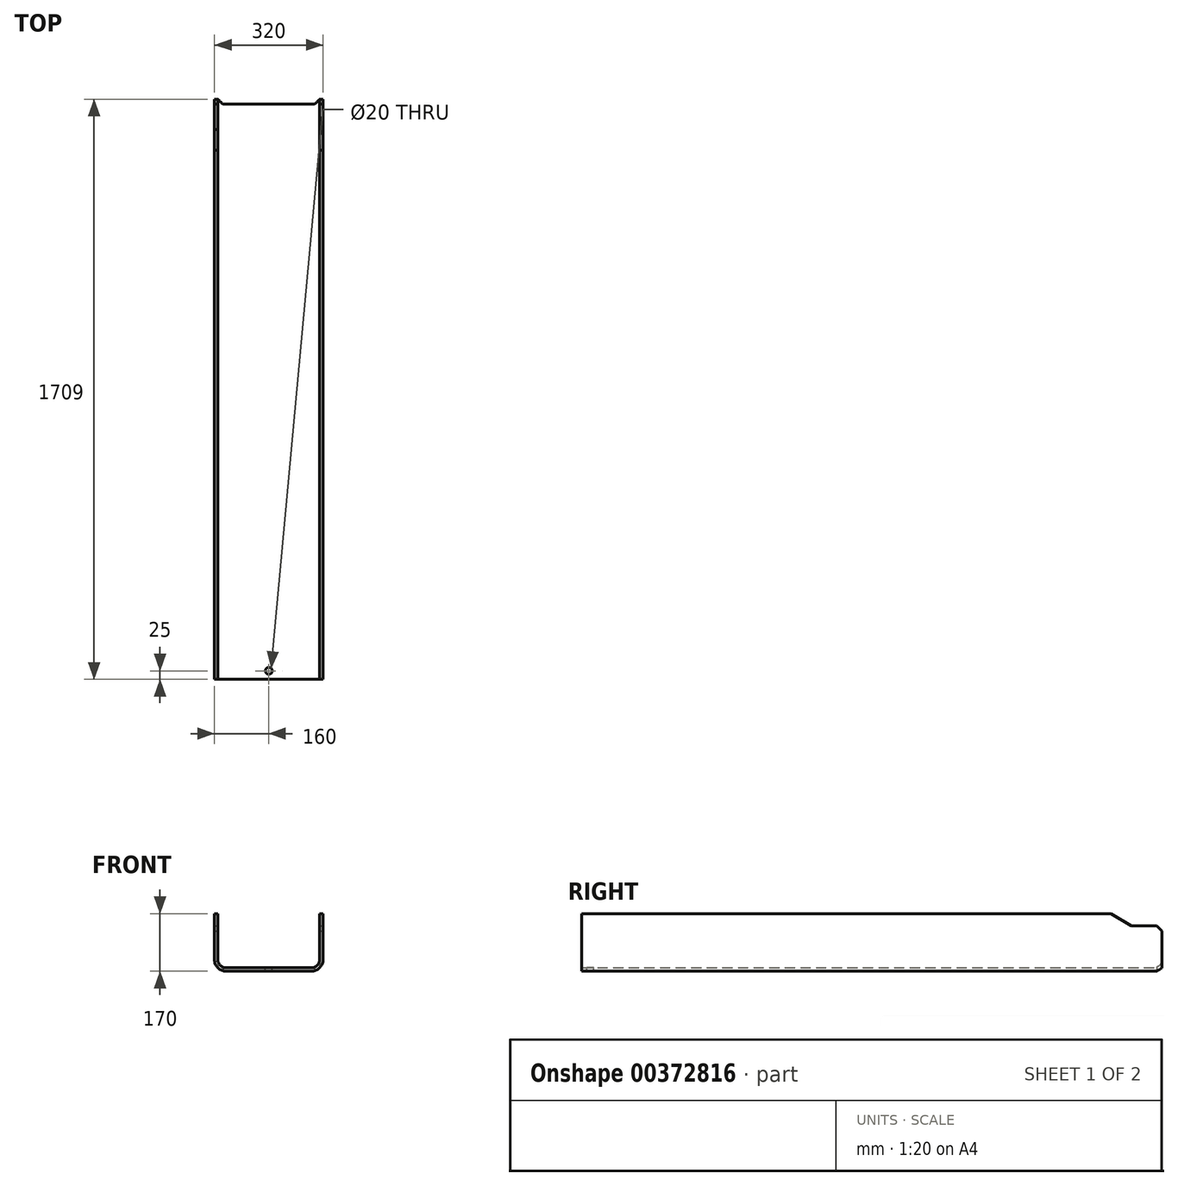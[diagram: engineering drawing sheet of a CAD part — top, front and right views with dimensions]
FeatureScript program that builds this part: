
annotation { "Feature Type Name" : "Feature", "Feature Type Description" : "" }
export const myFeature = defineFeature(function(context is Context, id is Id, definition is map)
    precondition{}
    {
        {
            var Q0;
            Q0=qCreatedBy(makeId("Front.planeOp"),FACE);
            var sketch = newSketch(context, id + "F0", { "sketchPlane" : qUnion([Q0])});
            skLineSegment(sketch, "E0", {"start": v(-160, 170) * mm, "end": v(-160, 0) * mm});
            skLineSegment(sketch, "E1", {"start": v(-160, 0) * mm, "end": v(160, 0) * mm});
            skLineSegment(sketch, "E2", {"start": v(160, 0) * mm, "end": v(160, 170) * mm});
            skLineSegment(sketch, "E3.0", {"start": v(150, 10) * mm, "end": v(150, 170) * mm});
            skLineSegment(sketch, "E3.1", {"start": v(-150, 10) * mm, "end": v(150, 10) * mm});
            skLineSegment(sketch, "E3.2", {"start": v(-150, 170) * mm, "end": v(-150, 10) * mm});
            skLineSegment(sketch, "E4", {"start": v(-160, 170) * mm, "end": v(-150, 170) * mm});
            skLineSegment(sketch, "E5", {"start": v(150, 170) * mm, "end": v(160, 170) * mm});
            skSolve(sketch);
        }
        {
            var Q0;
            Q0 = qSketchRegion(id + "F0", true);
            extrude(context, id + "F1", {"entities" : qUnion([Q0]), "endBound" : BoundingType.SYMMETRIC, "depth" : 1709 * mm});
        }
        {
            var Q0;
            Q0=makeQuery(id+"F1.opExtrude","SWEPT_EDGE",EDGE,{"disambiguationData":[OSD([sQuery(id+"F0.wireOp",EDGE,"E3.1"),sQuery(id+"F0.wireOp",EDGE,"E3.2")])]});
            var Q1;
            Q1=makeQuery(id+"F1.opExtrude","SWEPT_EDGE",EDGE,{"disambiguationData":[OSD([sQuery(id+"F0.wireOp",EDGE,"E3.0"),sQuery(id+"F0.wireOp",EDGE,"E3.1")])]});
            fillet(context, id + "F2", {"entities" : qUnion([Q0, Q1]), "radius" : 25 * mm, "tangentPropagation" : true, "allowEdgeOverflow" : false});
        }
        {
            var Q0;
            Q0=makeQuery(id+"F1.opExtrude","SWEPT_EDGE",EDGE,{"disambiguationData":[OSD([sQuery(id+"F0.wireOp",EDGE,"E1"),sQuery(id+"F0.wireOp",EDGE,"E2")])]});
            var Q1;
            Q1=makeQuery(id+"F1.opExtrude","SWEPT_EDGE",EDGE,{"disambiguationData":[OSD([sQuery(id+"F0.wireOp",EDGE,"E0"),sQuery(id+"F0.wireOp",EDGE,"E1")])]});
            fillet(context, id + "F3", {"entities" : qUnion([Q0, Q1]), "radius" : 35 * mm, "tangentPropagation" : true, "allowEdgeOverflow" : false});
        }
        {
            var Q0;
            Q0=makeQuery(id+"F1.opExtrude","SWEPT_FACE",FACE,{"disambiguationData":[OSD([sQuery(id+"F0.wireOp",EDGE,"E2")])]});
            var sketch = newSketch(context, id + "F4", { "sketchPlane" : qUnion([Q0])});
            skLineSegment(sketch, "E6", {"start": v(704.5, 170) * mm, "end": v(764.5, 134) * mm});
            skLineSegment(sketch, "E7", {"start": v(764.5, 134) * mm, "end": v(839.5, 134) * mm});
            skLineSegment(sketch, "E8", {"start": v(839.5, 134) * mm, "end": v(854.5, 119) * mm});
            skLineSegment(sketch, "E9", {"start": v(854.5, 119) * mm, "end": v(854.5, 170) * mm});
            skLineSegment(sketch, "E10", {"start": v(854.5, 170) * mm, "end": v(704.5, 170) * mm});
            skSolve(sketch);
        }
        {
            var Q0;
            Q0 = qSketchRegion(id + "F4", true);
            extrude(context, id + "F5", {"entities" : qUnion([Q0]), "operationType" : NewBodyOperationType.REMOVE, "endBound" : BoundingType.THROUGH_ALL, "oppositeDirection" : true, "depth" : 25 * mm});
        }
        {
            var Q0;
            Q0=makeQuery(id+"F1.opExtrude","SWEPT_FACE",FACE,{"disambiguationData":[OSD([sQuery(id+"F0.wireOp",EDGE,"E3.1")])]});
            var sketch = newSketch(context, id + "F6", { "sketchPlane" : qUnion([Q0])});
            skPoint(sketch, "E11", {"position": v(0, -829.5) * mm});
            skSolve(sketch);
        }
        {
            var Q0;
            Q0=sQuery(id+"F6.wireOp",VERTEX,"E11");
            var Q1;
            Q1=makeQuery(id+"F1.opExtrude","SWEPT_BODY",BODY,{"disambiguationData":[OSD([sQuery(id+"F0.wireOp",EDGE,"E0"),sQuery(id+"F0.wireOp",EDGE,"E1"),sQuery(id+"F0.wireOp",EDGE,"E2"),sQuery(id+"F0.wireOp",EDGE,"E3.0"),sQuery(id+"F0.wireOp",EDGE,"E3.1"),sQuery(id+"F0.wireOp",EDGE,"E3.2"),sQuery(id+"F0.wireOp",EDGE,"E4"),sQuery(id+"F0.wireOp",EDGE,"E5")])]});
            hole(context, id + "F7", {"style" : HoleStyle.SIMPLE, "endStyle" : HoleEndStyle.THROUGH, "holeDiameter" : 20 * mm, "isTappedThrough" : true, "tappedDepth" : 12 * mm, "tapClearance" : 3, "locations" : qUnion([Q0]), "scope" : qUnion([Q1])});
        }
        {
            var Q0;
            Q0=makeQuery(id+"F1.opExtrude","SWEPT_FACE",FACE,{"disambiguationData":[OSD([sQuery(id+"F0.wireOp",EDGE,"E3.1")])]});
            var sketch = newSketch(context, id + "F8", { "sketchPlane" : qUnion([Q0])});
            skLineSegment(sketch, "E12", {"start": v(-135, 839.5) * mm, "end": v(135, 839.5) * mm});
            skLineSegment(sketch, "E13", {"start": v(-135, 839.5) * mm, "end": v(-150, 854.5) * mm});
            skLineSegment(sketch, "E14", {"start": v(135, 839.5) * mm, "end": v(150, 854.5) * mm});
            skLineSegment(sketch, "E15", {"start": v(-150, 854.5) * mm, "end": v(150, 854.5) * mm});
            skSolve(sketch);
        }
        {
            var Q0;
            Q0 = qSketchRegion(id + "F8", true);
            extrude(context, id + "F9", {"entities" : qUnion([Q0]), "operationType" : NewBodyOperationType.REMOVE, "depth" : 30 * mm, "hasSecondDirection" : true, "secondDirectionOppositeDirection" : true, "secondDirectionDepth" : 10 * mm});
        }
    });
